# Revit family: 3-600-xx  37-600-xx - Peepers (Ceiling - Wall Mount)
name_source: partatom
category: Lighting Fixtures
revit_build: Autodesk Revit 2018 (Build: 20180423_1000(x64)
units: mm (PartAtom-declared; Revit-internal decimal feet)

## family parameters
Cut with Voids When Loaded = No
Host = Face
Light Source = Yes
Part Type = Normal
Room Calculation Point = No
Round Connector Dimension = Use Diameter
Shared = No

## types (3) — shared parameters
Color Filter = 16777215
Diffuser = Matte White Acrylic
Dimming Lamp Color Temperature Shift = <None>
Emit Shape Visible in Rendering = No
Emit from Circle Diameter = 3 "
Lamp = LED Array
Manufacturer = Oxygen Lighting
Model = 3-600-xx / 37-600-xx - Peepers
Other = <By Category>
Photometric Web File = 3-600-24 Peepers.ies
Tilt Angle = 90.00°
URL = www.oxygenlighting.com
Wattage Comments = 10.20 W at 120 V
zero-valued in all types: Default Elevation

## per-type parameters (varying)
| type | Metal Finish |
| 3-600-22 / 37-600-22 - Peepers | 22- Oiled Bronze |
| 3-600-24 / 37-600-24 - Peepers | 24 - Satin Nickel |
| 3-600-40 / 37-600-40 - Peepers | 40 - Aged Brass |

## geometry (parser evidence)
native form markers: Extrusion x1, Sweep x6
no freeform markers — native parametric forms only
